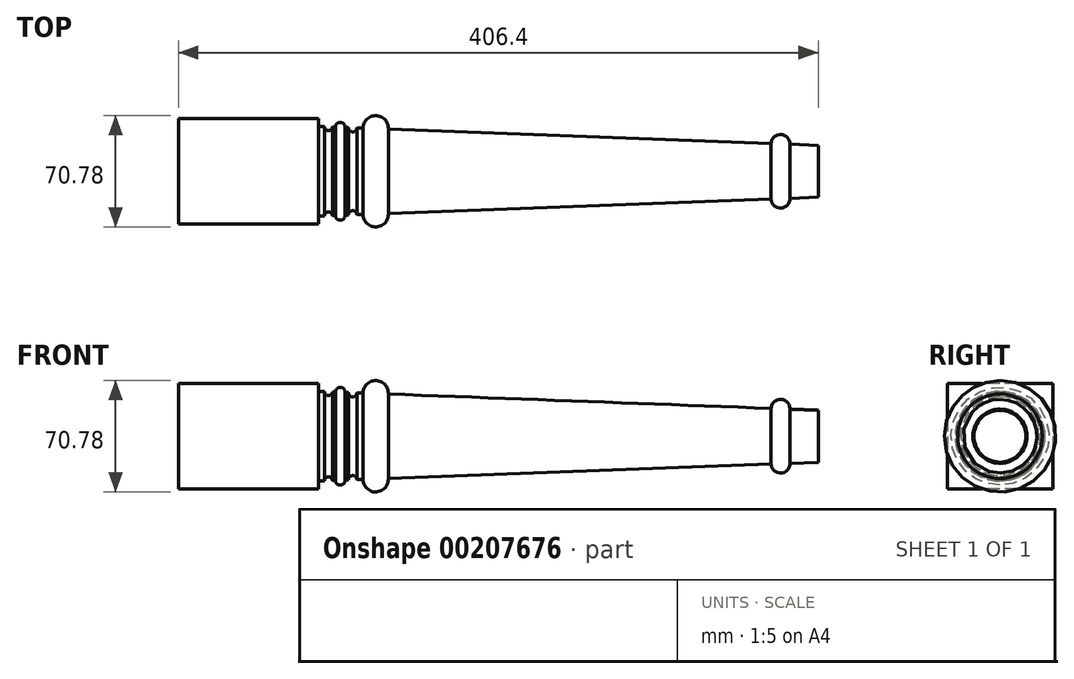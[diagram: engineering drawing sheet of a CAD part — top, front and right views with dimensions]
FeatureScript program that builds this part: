
annotation { "Feature Type Name" : "Feature", "Feature Type Description" : "" }
export const myFeature = defineFeature(function(context is Context, id is Id, definition is map)
    precondition{}
    {
        {
            var Q0;
            Q0=qCreatedBy(makeId("Front.planeOp"),FACE);
            var sketch = newSketch(context, id + "F0", { "sketchPlane" : qUnion([Q0])});
            skLineSegment(sketch, "E0", {"start": v(-53.74, 0) * mm, "end": v(-53.74, 28.5) * mm});
            skLineSegment(sketch, "E1", {"start": v(-53.74, 28.5) * mm, "end": v(263.76, 16.5) * mm});
            skLineSegment(sketch, "E2", {"start": v(263.76, 16.5) * mm, "end": v(263.76, 0) * mm});
            skLineSegment(sketch, "E3", {"start": v(263.76, 0) * mm, "end": v(-53.74, 0) * mm});
            skSolve(sketch);
        }
        {
            var Q0;
            Q0 = qSketchRegion(id + "F0", true);
            var Q1;
            Q1=sQuery(id+"F0.wireOp",EDGE,"E3");
            revolve(context, id + "F1", {"entities" : qUnion([Q0]), "axis" : qUnion([Q1]), "revolveType" : RevolveType.FULL});
        }
        {
            var Q0;
            Q0=makeQuery(id+"F1.opRevolve","SWEPT_FACE",FACE,{"disambiguationData":[OSD([sQuery(id+"F0.wireOp",EDGE,"E0")])]});
            var sketch = newSketch(context, id + "F2", { "sketchPlane" : qUnion([Q0])});
            skLineSegment(sketch, "E4.bottom", {"start": v(-33.5, 33.5) * mm, "end": v(33.5, 33.5) * mm});
            skLineSegment(sketch, "E4.top", {"start": v(-33.5, -33.5) * mm, "end": v(33.5, -33.5) * mm});
            skLineSegment(sketch, "E4.left", {"start": v(-33.5, 33.5) * mm, "end": v(-33.5, -33.5) * mm});
            skLineSegment(sketch, "E4.right", {"start": v(33.5, 33.5) * mm, "end": v(33.5, -33.5) * mm});
            skPoint(sketch, "E4.middle", {"position": v(0, 0) * mm});
            skSolve(sketch);
        }
        {
            var Q0;
            Q0=makeQuery(id+"F2.imprint","IMPRINT",FACE,{"disambiguationData":[TD([[makeQuery(id+"F2.imprint","IMPRINT",EDGE,{"derivedFrom":sQuery(id+"F2.wireOp",EDGE,"E4.bottom")}),-1.0]])]});
            var Q1;
            Q1=makeQuery(id+"F2.imprint","IMPRINT",FACE,{"disambiguationData":[TD([[makeQuery(id+"F2.imprint","IMPRINT",EDGE,{"derivedFrom":makeQuery(id+"F1.opRevolve","SWEPT_EDGE",EDGE,{"disambiguationData":[OSD([sQuery(id+"F0.wireOp",EDGE,"E0"),sQuery(id+"F0.wireOp",EDGE,"E1")])]})}),-1.0]])]});
            extrude(context, id + "F3", {"entities" : qUnion([Q0, Q1]), "operationType" : NewBodyOperationType.ADD, "depth" : 88.9 * mm});
        }
        {
            var Q0;
            Q0=qCreatedBy(makeId("Front.planeOp"),FACE);
            var sketch = newSketch(context, id + "F4", { "sketchPlane" : qUnion([Q0])});
            skCircle(sketch, "E5", {"center": v(239.73, 17.42) * mm, "radius": 5.98 * mm});
            skSolve(sketch);
        }
        {
            var Q0;
            Q0 = qSketchRegion(id + "F4", true);
            var Q1;
            Q1=makeQuery(id+"F1.opRevolve","SWEPT_FACE",FACE,{"disambiguationData":[OSD([sQuery(id+"F0.wireOp",EDGE,"E1")])]});
            revolve(context, id + "F5", {"operationType" : NewBodyOperationType.ADD, "entities" : qUnion([Q0]), "axis" : qUnion([Q1]), "revolveType" : RevolveType.FULL});
        }
        {
            var Q0;
            Q0=qCreatedBy(makeId("Front.planeOp"),FACE);
            var sketch = newSketch(context, id + "F6", { "sketchPlane" : qUnion([Q0])});
            skCircle(sketch, "E6", {"center": v(-17.44, 27.32) * mm, "radius": 8.06 * mm});
            skSolve(sketch);
        }
        {
            var Q0;
            Q0 = qSketchRegion(id + "F6", true);
            var Q1;
            Q1=sQuery(id+"F0.wireOp",EDGE,"E3");
            revolve(context, id + "F7", {"operationType" : NewBodyOperationType.ADD, "entities" : qUnion([Q0]), "axis" : qUnion([Q1]), "revolveType" : RevolveType.FULL});
        }
        {
            var Q0;
            Q0=qCreatedBy(makeId("Front.planeOp"),FACE);
            var sketch = newSketch(context, id + "F8", { "sketchPlane" : qUnion([Q0])});
            skCircle(sketch, "E7", {"center": v(-39.86, 28.1) * mm, "radius": 2.98 * mm});
            skSolve(sketch);
        }
        {
            var Q0;
            Q0 = qSketchRegion(id + "F8", true);
            var Q1;
            Q1=sQuery(id+"F0.wireOp",EDGE,"E3");
            revolve(context, id + "F9", {"operationType" : NewBodyOperationType.ADD, "entities" : qUnion([Q0]), "axis" : qUnion([Q1]), "revolveType" : RevolveType.FULL});
        }
        {
            var Q0;
            Q0=qCreatedBy(makeId("Front.planeOp"),FACE);
            var sketch = newSketch(context, id + "F10", { "sketchPlane" : qUnion([Q0])});
            skCircle(sketch, "E8", {"center": v(-47.43, 28.32) * mm, "radius": 2.56 * mm});
            skCircle(sketch, "E9", {"center": v(-32, 27.66) * mm, "radius": 2.67 * mm});
            skSolve(sketch);
        }
        {
            var Q0;
            Q0 = qSketchRegion(id + "F10", true);
            var Q1;
            {var subQ0=makeQuery(id+"F7.opRevolve","SWEPT_FACE",FACE,{"disambiguationData":[OSD([sQuery(id+"F6.wireOp",EDGE,"E6")])]});var subQ1=makeQuery(id+"F3.opExtrude","CAP_FACE",FACE,{"disambiguationData":[OSD([sQuery(id+"F2.wireOp",EDGE,"E4.bottom"),sQuery(id+"F2.wireOp",EDGE,"E4.top"),sQuery(id+"F2.wireOp",EDGE,"E4.left"),sQuery(id+"F2.wireOp",EDGE,"E4.right")])],"isStart":true});Q1=makeQuery(id+"F9.boolean.opBoolean","SPLIT",FACE,{"disambiguationData":[TD([subQ0])],"derivedFrom":makeQuery(id+"F7.boolean.opBoolean","SPLIT",FACE,{"disambiguationData":[TD([subQ1])],"derivedFrom":makeQuery(id+"F5.boolean.opBoolean","SPLIT",FACE,{"disambiguationData":[TD([subQ1])],"derivedFrom":makeQuery(id+"F1.opRevolve","SWEPT_FACE",FACE,{"disambiguationData":[OSD([sQuery(id+"F0.wireOp",EDGE,"E1")])]})})})});}
            revolve(context, id + "F11", {"operationType" : NewBodyOperationType.REMOVE, "entities" : qUnion([Q0]), "axis" : qUnion([Q1]), "revolveType" : RevolveType.FULL, "oppositeDirection" : true});
        }
    });
